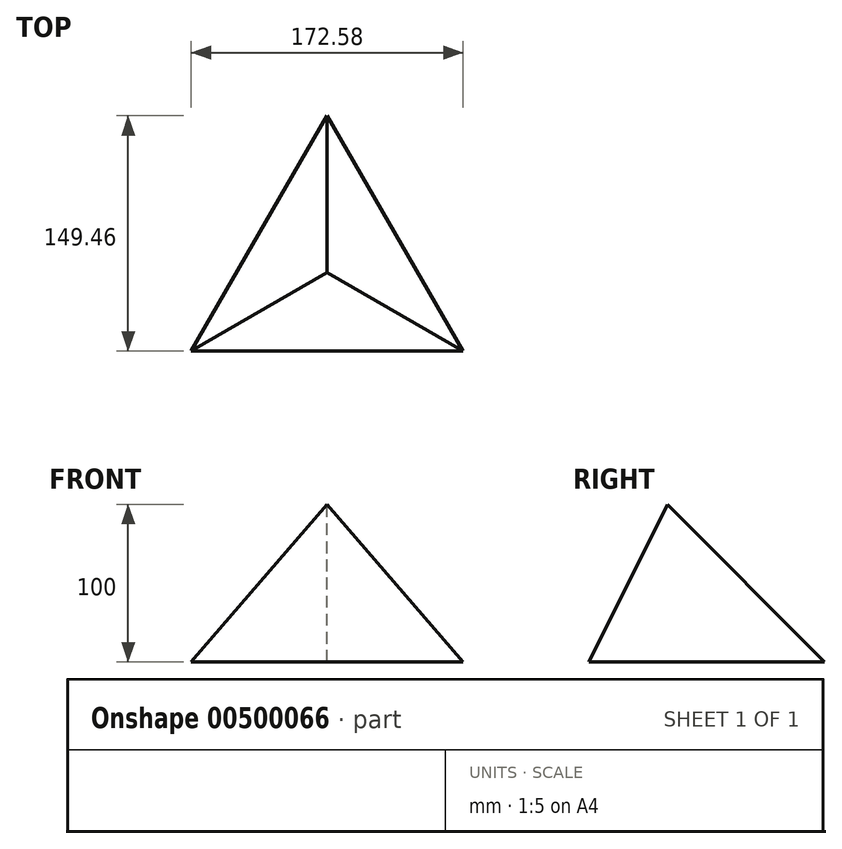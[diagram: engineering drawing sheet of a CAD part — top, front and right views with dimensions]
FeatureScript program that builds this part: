
annotation { "Feature Type Name" : "Feature", "Feature Type Description" : "" }
export const myFeature = defineFeature(function(context is Context, id is Id, definition is map)
    precondition{}
    {
        {
            var Q0;
            Q0=qCreatedBy(makeId("Top.planeOp"),FACE);
            var sketch = newSketch(context, id + "F0", { "sketchPlane" : qUnion([Q0])});
            skCircle(sketch, "E0.cCircle", {"center": v(0, 0) * mm, "radius": 99.64 * mm, "construction": true});
            skLineSegment(sketch, "E0.0", {"start": v(0, 99.64) * mm, "end": v(86.3, -49.82) * mm});
            skLineSegment(sketch, "E0.1", {"start": v(86.3, -49.82) * mm, "end": v(-86.3, -49.82) * mm});
            skLineSegment(sketch, "E0.2", {"start": v(-86.3, -49.82) * mm, "end": v(0, 99.64) * mm});
            skSolve(sketch);
        }
        {
            var Q0;
            Q0=qCreatedBy(makeId("Top.planeOp"),FACE);
            cPlane(context, id + "F1", {"entities" : qUnion([Q0]), "cplaneType" : CPlaneType.OFFSET, "offset" : 100 * mm, "width" : 152.4 * mm, "height" : 152.4 * mm});
        }
        {
            var Q0;
            Q0=qCreatedBy(id+"F1.planeOp",FACE);
            var sketch = newSketch(context, id + "F2", { "sketchPlane" : qUnion([Q0])});
            skPoint(sketch, "E1", {"position": v(0, 0) * mm});
            skSolve(sketch);
        }
        {
            var Q0;
            Q0=makeQuery(id+"F0.imprint","IMPRINT",FACE,{"disambiguationData":[TD([[makeQuery(id+"F0.imprint","IMPRINT",EDGE,{"derivedFrom":sQuery(id+"F0.wireOp",EDGE,"E0.0")}),-1.0]])]});
            var Q1;
            Q1=sQuery(id+"F2.wireOp",VERTEX,"E1");
            loft(context, id + "F3", {"sheetProfilesArray" : [{ "sheetProfileEntities" : qUnion([Q0]) }, { "sheetProfileEntities" : qUnion([Q1]) }]});
        }
    });
